# Revit family: Valve_Zip_Horne_TMV_Box_PipesOneEnd
name_source: partatom
category: Specialty Equipment
revit_build: Autodesk Revit 2018 (Build: 20190510_1515(x64)
units: mm (PartAtom-declared; Revit-internal decimal feet)

## family parameters
Always vertical = Yes
Cut with Voids When Loaded = Yes
OmniClass Number = 23.65.55.14.24
OmniClass Title = Mixing Valves for Liquid Services
Part Type = Normal
Room Calculation Point = No
Round Connector Dimension = Use Diameter
Shared = No
Work Plane-Based = No

## types (2) — shared parameters
Manufacturer = Zip Australia
ManufacturerOverallDepth = 74 mm
ManufacturerOverallHeight = 370 mm  [stored 1.21391 ft]
ManufacturerOverallWidth = 370 mm  [stored 1.21391 ft]
ManufacturerURLProductSpecific = https://www.zipwater.com
Material = Metal_BrushedChrome_Zip
ModifiedIssue = 20210225 $
URL = https://www.zipwater.com

## per-type parameters (varying)
| type | Description | HingedDoor | ManufacturerSpecCode | Model | RemoveableDoor | Type Comments |
| Removable Door (42157) | Horne TMV Model H1502: Recessed pre-plumbed box configuration with lockable flat stainless steel removable door - pipes at one end | No | 42157 | Horne TMV  H1502 Brass in box Configuration - Removable Door | Yes | Removable Door |
| Hinged Door (42457) | Horne TMV Model H1502: Recessed pre-plumbed box configuration with lockable Hinged stainless steel door - pipes at one end | Yes | 42457 | Horne TMV  H1502 Brass in box Configuration - Hinged Door | No | Hinged Door |

note: [stored X ft] marks values corroborated as IEEE doubles in the binary element streams (Revit-internal decimal feet)

## geometry (parser evidence)
native form markers: Sweep x5
no freeform markers — native parametric forms only
